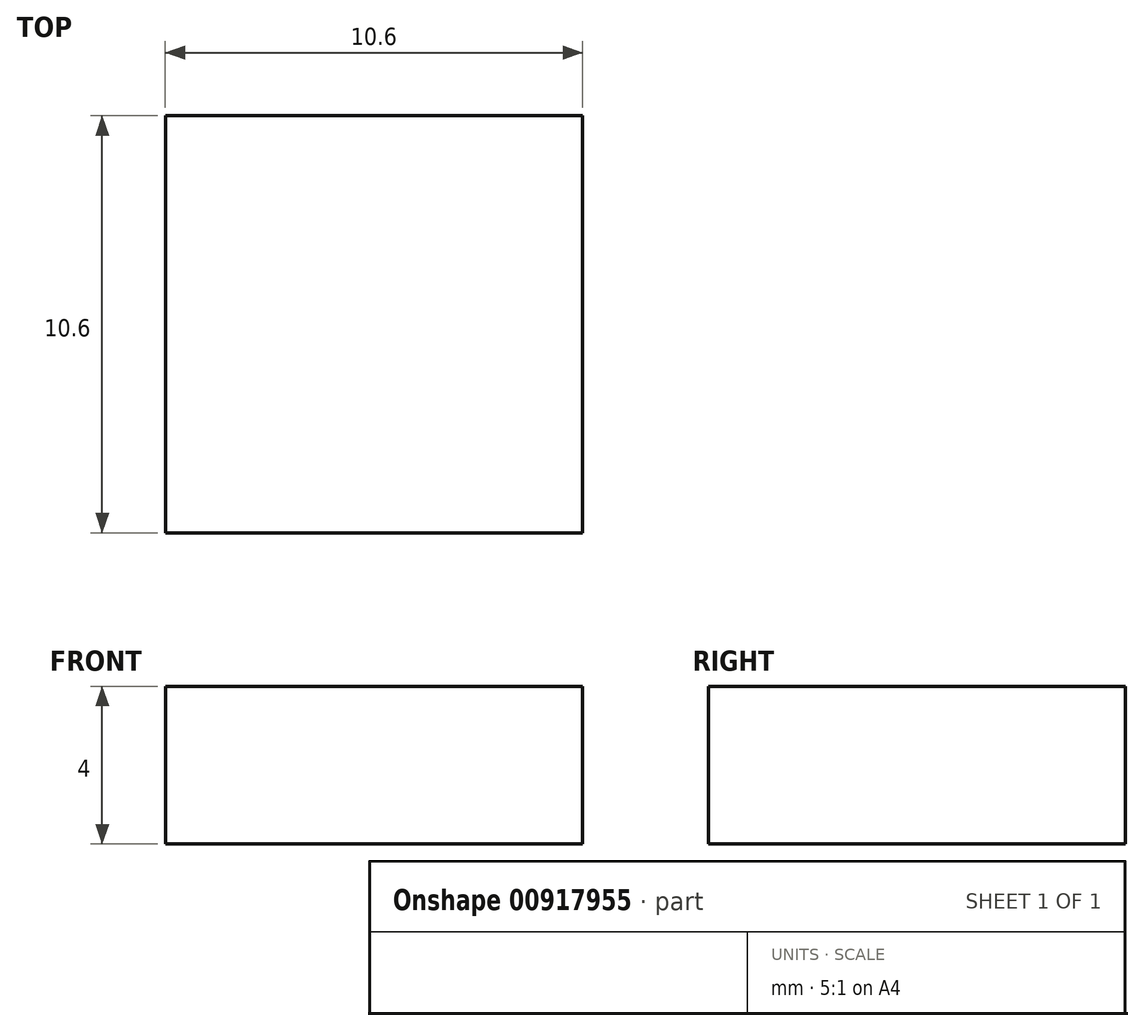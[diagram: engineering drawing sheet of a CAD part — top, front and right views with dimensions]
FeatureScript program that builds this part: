
annotation { "Feature Type Name" : "Feature", "Feature Type Description" : "" }
export const myFeature = defineFeature(function(context is Context, id is Id, definition is map)
    precondition{}
    {
        {
            var Q0;
            Q0=qCreatedBy(makeId("Top.planeOp"),FACE);
            var sketch = newSketch(context, id + "F0", { "sketchPlane" : qUnion([Q0])});
            skLineSegment(sketch, "E0.bottom", {"start": v(-8.5, 4.1) * mm, "end": v(2.1, 4.1) * mm});
            skLineSegment(sketch, "E0.top", {"start": v(-8.5, -6.5) * mm, "end": v(2.1, -6.5) * mm});
            skLineSegment(sketch, "E0.left", {"start": v(-8.5, 4.1) * mm, "end": v(-8.5, -6.5) * mm});
            skLineSegment(sketch, "E0.right", {"start": v(2.1, 4.1) * mm, "end": v(2.1, -6.5) * mm});
            skSolve(sketch);
        }
        {
            var Q0;
            Q0=makeQuery(id+"F0.imprint","IMPRINT",FACE,{"disambiguationData":[TD([[makeQuery(id+"F0.imprint","IMPRINT",EDGE,{"derivedFrom":sQuery(id+"F0.wireOp",EDGE,"E0.bottom")}),-1.0]])]});
            extrude(context, id + "F1", {"entities" : qUnion([Q0]), "depth" : 4 * mm, "offsetDistance" : 25.4 * mm});
        }
    });
